# Revit family: Detail-Connection-Steel & Tube-HST Standard Cleat with Bolts-Side
name_source: partatom
category: Detail Items
revit_build: Autodesk Revit 2017 (Build: 20170118_1100(x64)
units: mm (PartAtom-declared; Revit-internal decimal feet)

## family parameters
OmniClass Number = 23.35.20.14.11.14
OmniClass Title = Sheet Metal Roofing
Rotate with component = No
Section Shape = Not Defined
Shared = No

## types (7) — shared parameters
Assembly Code = B1020230
CBICode = 3411
CBIDescription = Structural steelwork
Description = HST Steel Purlins and Girts are high strength lipped profile sections, providing an economic solution for your building project.
Manufacturer = Steel & Tube
ManufacturerName = Steel & Tube
ManufacturerURL = http://www.steelandtube.co.nz
ModifiedIssue_ANZRS = 20160520 $
SpecificationDescription = Steel & Tube Purlins & Girts
SpecificationReference = 3411ST
Type Comments = HST Standard Cleat with Bolts-Side
URL = http://www.steelandtube.co.nz
Uniclass2015Code = Pr_20_76_51_21
Uniclass2015Title = Cold-formed galvanized steel sections
Uniclass2015Version = 2015

## per-type parameters (varying)
| type | Beam Size | Bolt Row2 Validation | Height_ANZRS | f | g |
| HST100 | 102 mm | 500 mm  [stored 1.64042 ft] | 100 mm  [stored 0.328084 ft] | 57 mm  [stored 0.187008 ft] | 64 mm  [stored 0.209974 ft] |
| HST150 | 152 mm  [stored 0.498688 ft] | 80 mm  [stored 0.262467 ft] | 150 mm | 41 mm  [stored 0.134514 ft] | 80 mm  [stored 0.262467 ft] |
| HST200 | 203 mm  [stored 0.66601 ft] | 120 mm  [stored 0.393701 ft] | 200 mm  [stored 0.656168 ft] | 48 mm  [stored 0.15748 ft] | 120 mm  [stored 0.393701 ft] |
| HST250 | 250 mm  [stored 0.82021 ft] | 160 mm  [stored 0.524934 ft] | 250 mm  [stored 0.82021 ft] | 53 mm  [stored 0.173885 ft] | 160 mm  [stored 0.524934 ft] |
| HST300 | 300 mm | 200 mm  [stored 0.656168 ft] | 300 mm | 55 mm  [stored 0.180446 ft] | 200 mm  [stored 0.656168 ft] |
| HST350 | 350 mm  [stored 1.14829 ft] | 240 mm  [stored 0.787402 ft] | 340 mm  [stored 1.11549 ft] | 60 mm  [stored 0.19685 ft] | 240 mm  [stored 0.787402 ft] |
| HST400 | 400 mm | 280 mm  [stored 0.918635 ft] | 380 mm | 70 mm  [stored 0.229659 ft] | 280 mm  [stored 0.918635 ft] |

note: column(s) folded — value = type name in every type: Model

note: [stored X ft] marks values corroborated as IEEE doubles in the binary element streams (Revit-internal decimal feet)

## geometry (parser evidence)
native form markers: Sweep x2
no freeform markers — native parametric forms only
